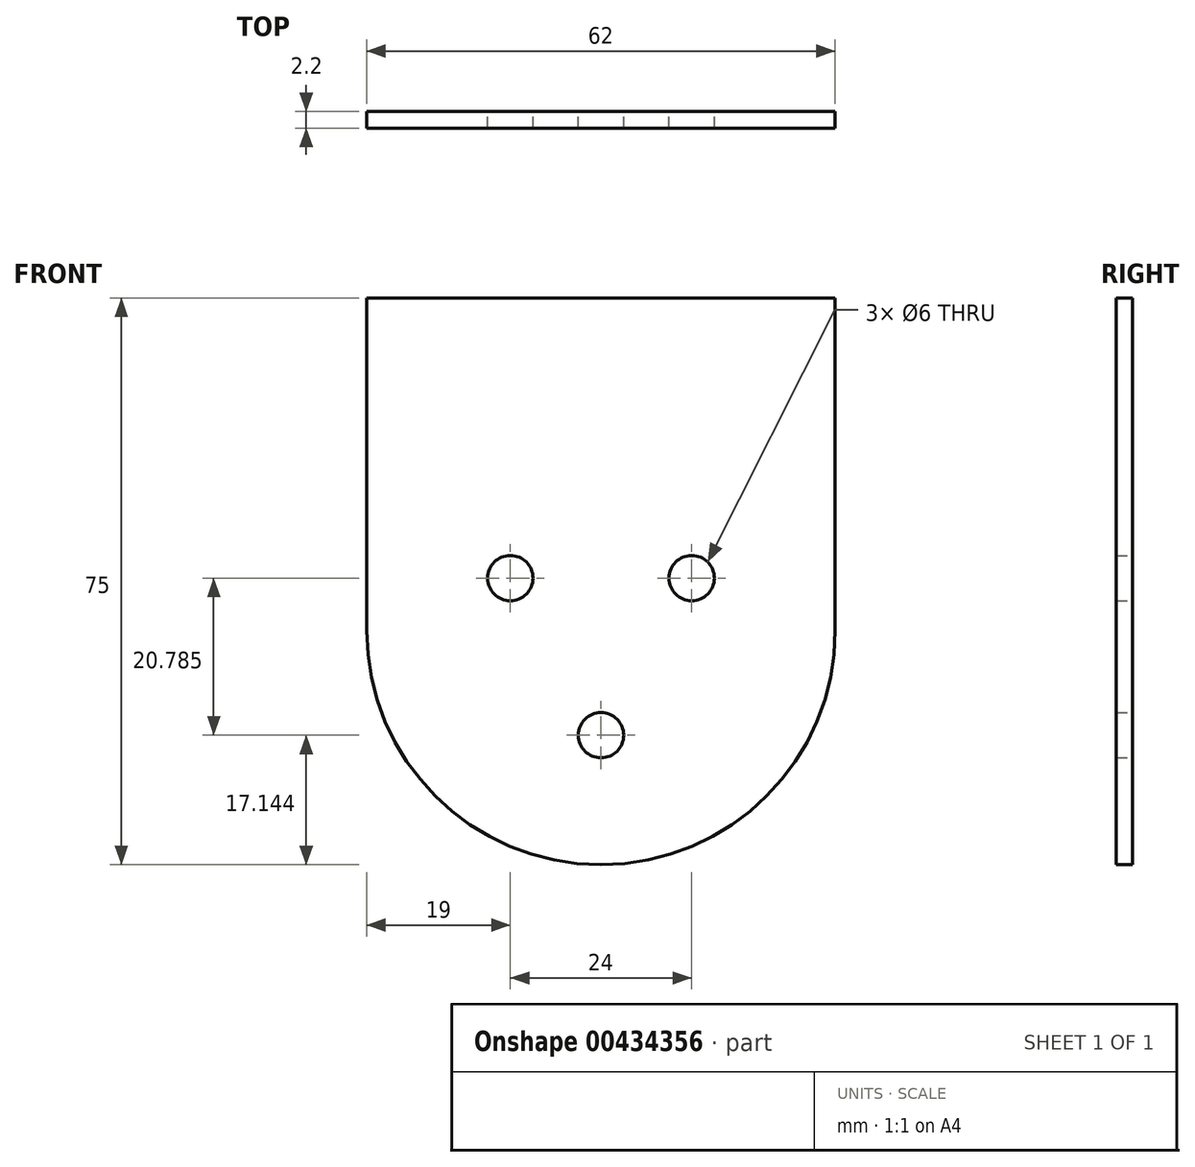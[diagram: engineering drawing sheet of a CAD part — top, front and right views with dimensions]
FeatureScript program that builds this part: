
annotation { "Feature Type Name" : "Feature", "Feature Type Description" : "" }
export const myFeature = defineFeature(function(context is Context, id is Id, definition is map)
    precondition{}
    {
        {
            var Q0;
            Q0=qCreatedBy(makeId("Front.planeOp"),FACE);
            var sketch = newSketch(context, id + "F0", { "sketchPlane" : qUnion([Q0])});
            skArc(sketch, "E0", {"start": v(0, -31) * mm, "mid": v(21.92, -21.92) * mm, "end": v(31, 0) * mm});
            skLineSegment(sketch, "E1", {"start": v(31, 0) * mm, "end": v(31, 44) * mm});
            skLineSegment(sketch, "E2", {"start": v(0, -44.96) * mm, "end": v(0, 184.97) * mm, "construction": true});
            skArc(sketch, "E3.1.0", {"start": v(9.4, 5.43) * mm, "mid": v(10.5, 9.53) * mm, "end": v(14.6, 8.43) * mm});
            skArc(sketch, "E3.1.1", {"start": v(9.4, 5.43) * mm, "mid": v(13.5, 4.33) * mm, "end": v(14.6, 8.43) * mm});
            skPoint(sketch, "E3.center", {"position": v(0, 28) * mm});
            skLineSegment(sketch, "E4", {"start": v(0, 0) * mm, "end": v(12, 6.93) * mm, "construction": true});
            skArc(sketch, "E5", {"start": v(0, -31) * mm, "mid": v(31, 0) * mm, "end": v(0, 31) * mm, "construction": true});
            skPoint(sketch, "E6.MirrorCS.end.orphan", {"position": v(0, -16.86) * mm});
            skPoint(sketch, "E7.MirrorP", {"position": v(0, -10.86) * mm});
            skArc(sketch, "E8.MirrorCS", {"start": v(-9.4, 5.43) * mm, "mid": v(-10.5, 9.53) * mm, "end": v(-14.6, 8.43) * mm});
            skArc(sketch, "E9.MirrorCS", {"start": v(-9.4, 5.43) * mm, "mid": v(-13.5, 4.33) * mm, "end": v(-14.6, 8.43) * mm});
            skLineSegment(sketch, "E10.MirrorCS", {"start": v(0, 0) * mm, "end": v(-12, 6.93) * mm, "construction": true});
            skArc(sketch, "E11.MirrorCS", {"start": v(0, -31) * mm, "mid": v(-21.92, -21.92) * mm, "end": v(-31, 0) * mm});
            skArc(sketch, "E12.MirrorCS", {"start": v(0, -31) * mm, "mid": v(-31, 0) * mm, "end": v(0, 31) * mm, "construction": true});
            skLineSegment(sketch, "E13.MirrorCS", {"start": v(-31, 0) * mm, "end": v(-31, 44) * mm});
            skCircle(sketch, "E14", {"center": v(0, 0) * mm, "radius": 13.86 * mm, "construction": true});
            skCircle(sketch, "E15", {"center": v(0, -13.86) * mm, "radius": 3 * mm});
            skLineSegment(sketch, "E16", {"start": v(-43.13, 44) * mm, "end": v(51.96, 44) * mm, "construction": true});
            skLineSegment(sketch, "E17", {"start": v(-31, 44) * mm, "end": v(31, 44) * mm});
            skSolve(sketch);
        }
        {
            var Q0;
            Q0 = qSketchRegion(id + "F0", true);
            extrude(context, id + "F1", {"entities" : qUnion([Q0]), "depth" : 2.2 * mm});
        }
    });
